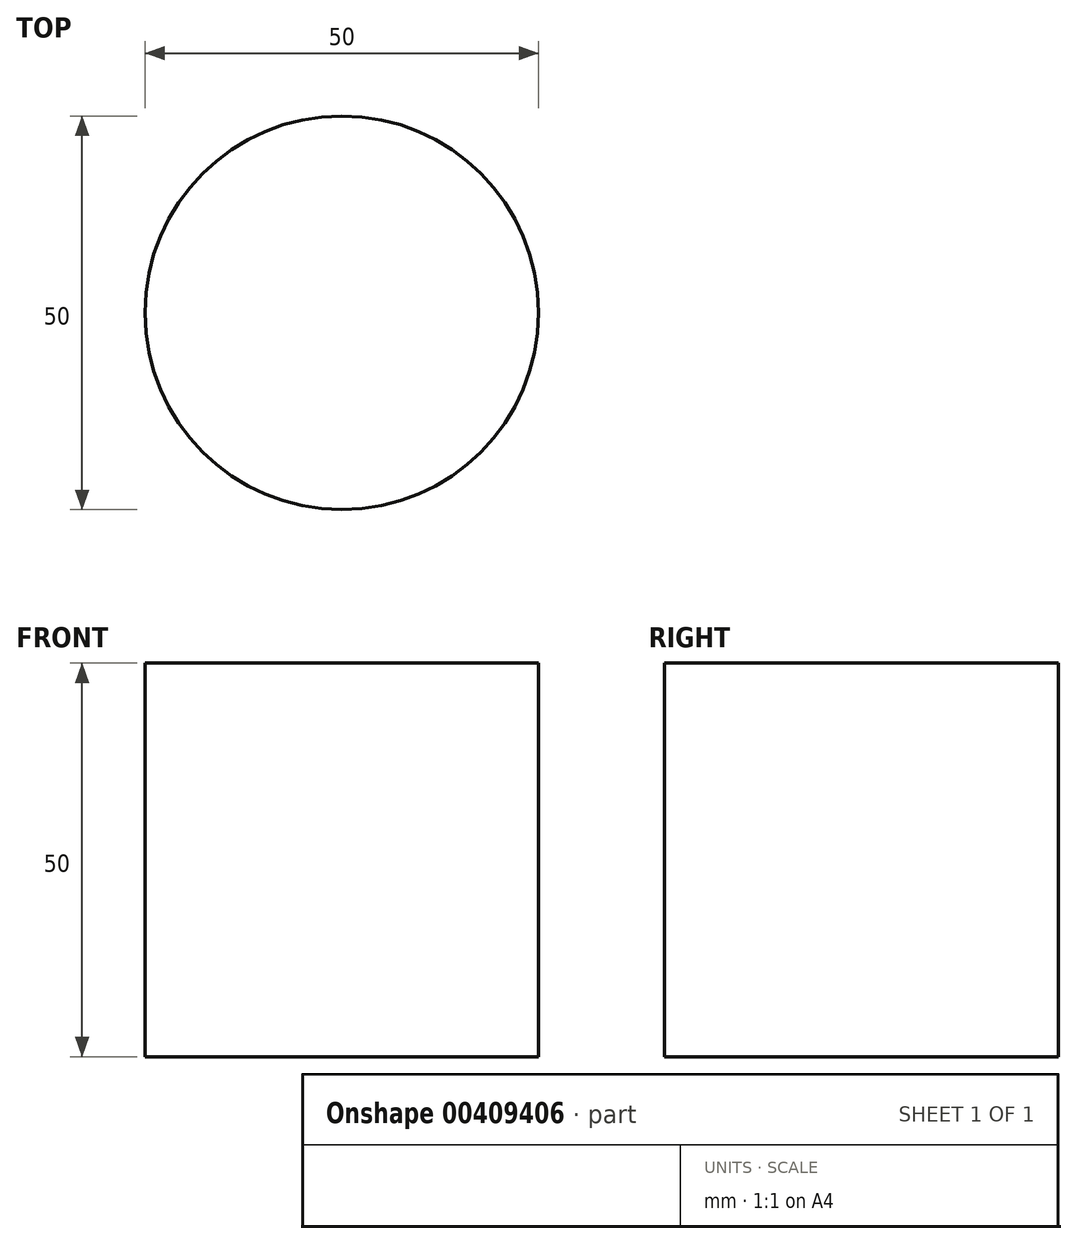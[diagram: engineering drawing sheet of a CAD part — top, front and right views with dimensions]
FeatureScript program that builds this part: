
annotation { "Feature Type Name" : "Feature", "Feature Type Description" : "" }
export const myFeature = defineFeature(function(context is Context, id is Id, definition is map)
    precondition{}
    {
        {
            var Q0;
            Q0=qCreatedBy(makeId("Top.planeOp"),FACE);
            var sketch = newSketch(context, id + "F0", { "sketchPlane" : qUnion([Q0])});
            skCircle(sketch, "E0", {"center": v(0, 0) * mm, "radius": 25 * mm});
            skSolve(sketch);
        }
        {
            var Q0;
            Q0 = qSketchRegion(id + "F0", true);
            extrude(context, id + "F1", {"entities" : qUnion([Q0]), "depth" : 50 * mm});
        }
    });
